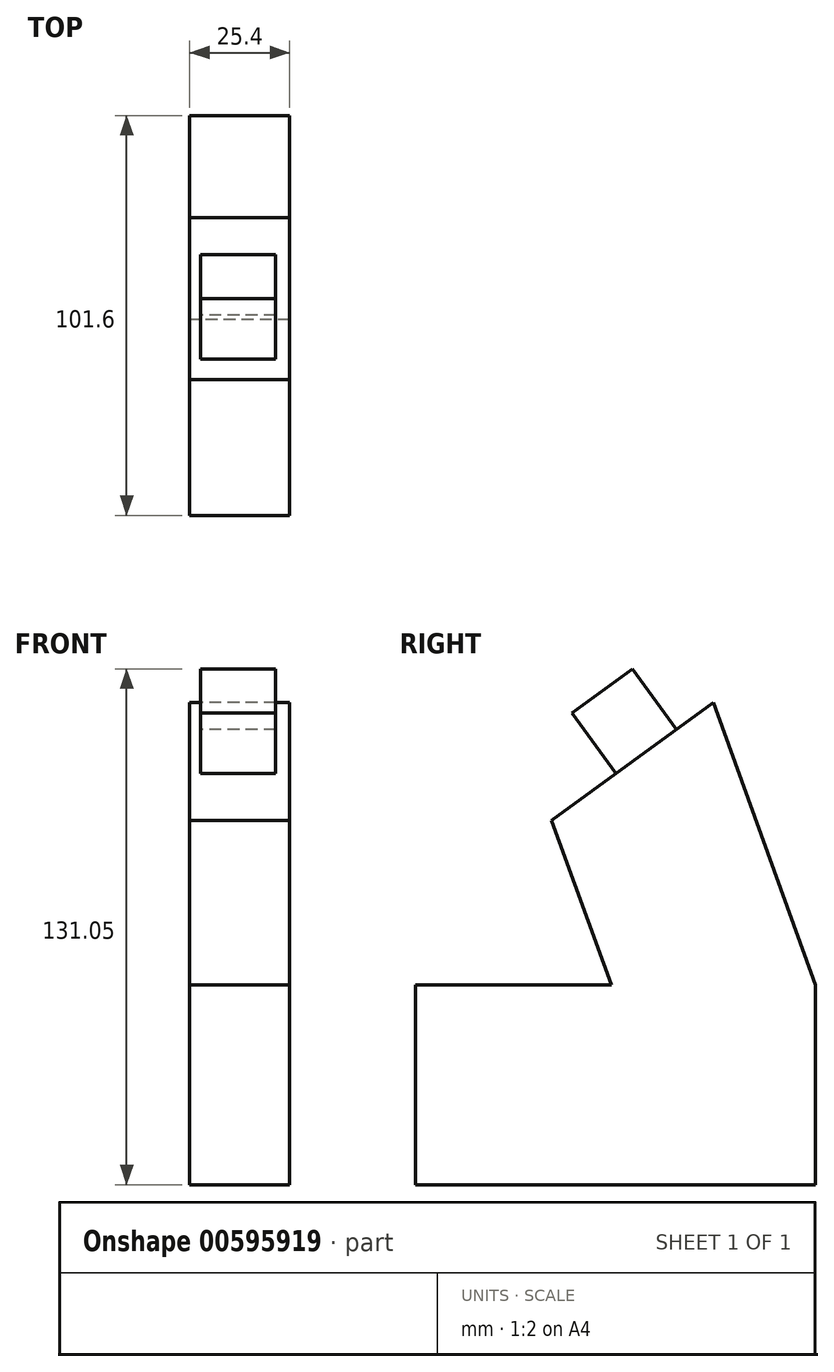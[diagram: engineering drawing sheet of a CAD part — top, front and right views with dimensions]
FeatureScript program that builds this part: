
annotation { "Feature Type Name" : "Feature", "Feature Type Description" : "" }
export const myFeature = defineFeature(function(context is Context, id is Id, definition is map)
    precondition{}
    {
        {
            var Q0;
            Q0=qCreatedBy(makeId("Right.planeOp"),FACE);
            var sketch = newSketch(context, id + "F0", { "sketchPlane" : qUnion([Q0])});
            skLineSegment(sketch, "E0.bottom", {"start": v(-101.6, 0) * mm, "end": v(0, 0) * mm});
            skLineSegment(sketch, "E0.top", {"start": v(-101.6, -50.8) * mm, "end": v(0, -50.8) * mm});
            skLineSegment(sketch, "E0.left", {"start": v(-101.6, 0) * mm, "end": v(-101.6, -50.8) * mm});
            skLineSegment(sketch, "E0.right", {"start": v(0, 0) * mm, "end": v(0, -50.8) * mm});
            skLineSegment(sketch, "E1", {"start": v(0, 0) * mm, "end": v(-25.94, 71.65) * mm});
            skLineSegment(sketch, "E2", {"start": v(-25.94, 71.65) * mm, "end": v(-67.05, 41.8) * mm});
            skLineSegment(sketch, "E3", {"start": v(-67.05, 41.8) * mm, "end": v(-51.91, 0) * mm});
            skSolve(sketch);
        }
        {
            var Q0;
            {var subQ0=sQuery(id+"F0.wireOp",EDGE,"E1");Q0=makeQuery(id+"F0.imprint","IMPRINT",FACE,{"disambiguationData":[TD([[makeQuery(id+"F0.imprint","IMPRINT",EDGE,{"derivedFrom":subQ0}),1.0]])]});}
            var Q1;
            Q1=makeQuery(id+"F0.imprint","IMPRINT",FACE,{"disambiguationData":[TD([[makeQuery(id+"F0.imprint","IMPRINT",EDGE,{"derivedFrom":sQuery(id+"F0.wireOp",EDGE,"E0.top")}),1.0]])]});
            extrude(context, id + "F1", {"entities" : qUnion([Q0, Q1]), "depth" : 25.4 * mm, "offsetDistance" : 25.4 * mm});
        }
        {
            var Q0;
            Q0=makeQuery(id+"F1.opExtrude","SWEPT_FACE",FACE,{"disambiguationData":[OSD([sQuery(id+"F0.wireOp",EDGE,"E2")])]});
            var sketch = newSketch(context, id + "F2", { "sketchPlane" : qUnion([Q0])});
            skLineSegment(sketch, "E4.bottom", {"start": v(21.8, -9.53) * mm, "end": v(2.75, -9.52) * mm});
            skLineSegment(sketch, "E4.top", {"start": v(21.8, 9.52) * mm, "end": v(2.75, 9.52) * mm});
            skLineSegment(sketch, "E4.left", {"start": v(21.8, -9.52) * mm, "end": v(21.8, 9.53) * mm});
            skLineSegment(sketch, "E4.right", {"start": v(2.75, -9.53) * mm, "end": v(2.75, 9.53) * mm});
            skPoint(sketch, "E4.middle", {"position": v(12.27, 0) * mm});
            skSolve(sketch);
        }
        {
            var Q0;
            Q0=makeQuery(id+"F2.imprint","IMPRINT",FACE,{"disambiguationData":[TD([[makeQuery(id+"F2.imprint","IMPRINT",EDGE,{"derivedFrom":sQuery(id+"F2.wireOp",EDGE,"E4.bottom")}),-1.0]])]});
            extrude(context, id + "F3", {"entities" : qUnion([Q0]), "operationType" : NewBodyOperationType.ADD, "depth" : 19.05 * mm, "offsetDistance" : 25.4 * mm});
        }
    });
